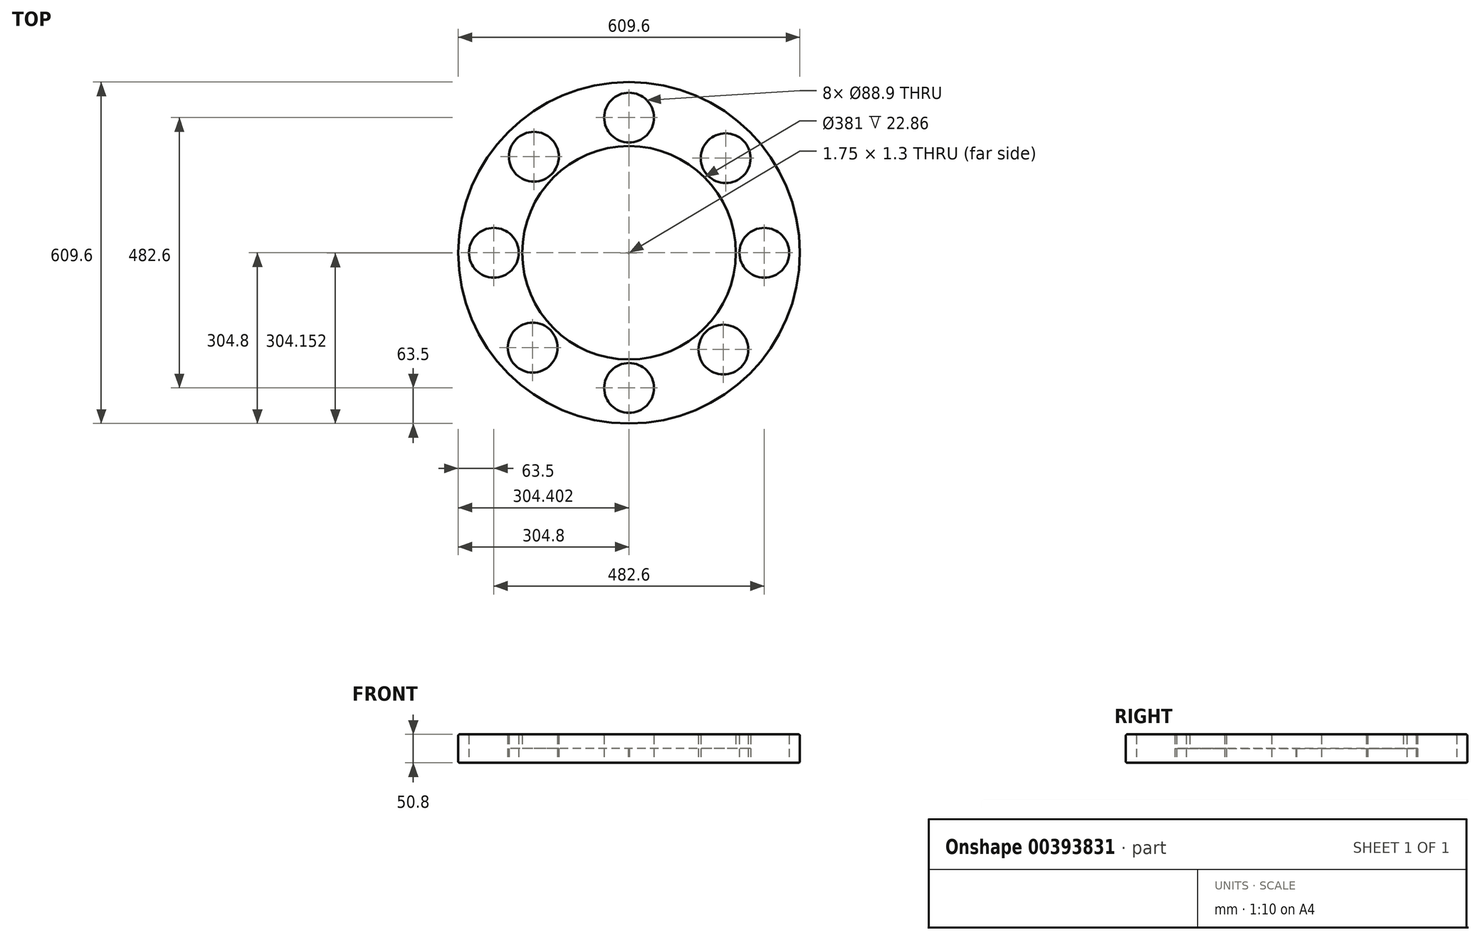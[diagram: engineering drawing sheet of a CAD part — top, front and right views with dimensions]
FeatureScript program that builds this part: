
annotation { "Feature Type Name" : "Feature", "Feature Type Description" : "" }
export const myFeature = defineFeature(function(context is Context, id is Id, definition is map)
    precondition{}
    {
        {
            var Q0;
            Q0=qCreatedBy(makeId("Top.planeOp"),FACE);
            var sketch = newSketch(context, id + "F0", { "sketchPlane" : qUnion([Q0])});
            skCircle(sketch, "E0", {"center": v(0, 0) * mm, "radius": 304.8 * mm});
            skCircle(sketch, "E1", {"center": v(0, 0) * mm, "radius": 190.5 * mm});
            skCircle(sketch, "E2", {"center": v(0, 241.3) * mm, "radius": 44.45 * mm});
            skCircle(sketch, "E3", {"center": v(241.3, 0) * mm, "radius": 44.45 * mm});
            skCircle(sketch, "E4", {"center": v(0, -241.3) * mm, "radius": 44.45 * mm});
            skCircle(sketch, "E5", {"center": v(-241.3, 0) * mm, "radius": 44.45 * mm});
            skCircle(sketch, "E6", {"center": v(-169.71, 171.53) * mm, "radius": 44.45 * mm});
            skCircle(sketch, "E7", {"center": v(172.4, 168.83) * mm, "radius": 44.45 * mm});
            skCircle(sketch, "E8", {"center": v(168.42, -172.8) * mm, "radius": 44.45 * mm});
            skCircle(sketch, "E9", {"center": v(-171.93, -169.3) * mm, "radius": 44.45 * mm});
            skLineSegment(sketch, "E10", {"start": v(0, 241.3) * mm, "end": v(0, 304.8) * mm});
            skLineSegment(sketch, "E11", {"start": v(241.3, 0) * mm, "end": v(304.8, 0) * mm});
            skLineSegment(sketch, "E12", {"start": v(0, -241.3) * mm, "end": v(0, -304.8) * mm});
            skLineSegment(sketch, "E13", {"start": v(-241.3, 0) * mm, "end": v(-304.8, 0) * mm});
            skLineSegment(sketch, "E14", {"start": v(0, 304.8) * mm, "end": v(0, -304.8) * mm});
            skLineSegment(sketch, "E15", {"start": v(-304.8, 0) * mm, "end": v(304.8, 0) * mm});
            skLineSegment(sketch, "E16", {"start": v(-169.71, 171.53) * mm, "end": v(168.42, -172.8) * mm});
            skLineSegment(sketch, "E17", {"start": v(172.4, 168.83) * mm, "end": v(-171.93, -169.3) * mm});
            skSolve(sketch);
        }
        {
            var Q0;
            Q0 = qSketchRegion(id + "F0", true);
            extrude(context, id + "F1", {"entities" : qUnion([Q0]), "depth" : 50.8 * mm});
        }
        {
            var Q0;
            Q0=makeQuery(id+"F0.imprint","IMPRINT",FACE,{"disambiguationData":[TD([[makeQuery(id+"F0.imprint","IMPRINT",EDGE,{"derivedFrom":sQuery(id+"F0.wireOp",EDGE,"E9")}),1.0]])]});
            var Q1;
            {var subQ0=sQuery(id+"F0.wireOp",EDGE,"E15");var subQ4=makeQuery(id+"F0.imprint","IMPRINT",VERTEX,{"disambiguationData":[OD(0.0)],"derivedFrom":subQ0});Q1=makeQuery(id+"F0.imprint","IMPRINT",FACE,{"disambiguationData":[TD([[makeQuery(id+"F0.imprint","IMPRINT",EDGE,{"disambiguationData":[TD([[subQ4,1.0]])],"derivedFrom":subQ0}),-1.0]])]});}
            var Q2;
            {var subQ0=sQuery(id+"F0.wireOp",EDGE,"E15");var subQ4=makeQuery(id+"F0.imprint","IMPRINT",VERTEX,{"disambiguationData":[OD(0.0)],"derivedFrom":subQ0});Q2=makeQuery(id+"F0.imprint","IMPRINT",FACE,{"disambiguationData":[TD([[makeQuery(id+"F0.imprint","IMPRINT",EDGE,{"disambiguationData":[TD([[subQ4,1.0]])],"derivedFrom":subQ0}),1.0]])]});}
            var Q3;
            Q3=makeQuery(id+"F0.imprint","IMPRINT",FACE,{"disambiguationData":[TD([[makeQuery(id+"F0.imprint","IMPRINT",EDGE,{"derivedFrom":sQuery(id+"F0.wireOp",EDGE,"E6")}),1.0]])]});
            var Q4;
            {var subQ0=sQuery(id+"F0.wireOp",EDGE,"E14");var subQ4=makeQuery(id+"F0.imprint","IMPRINT",VERTEX,{"disambiguationData":[OD(0.0)],"derivedFrom":subQ0});Q4=makeQuery(id+"F0.imprint","IMPRINT",FACE,{"disambiguationData":[TD([[makeQuery(id+"F0.imprint","IMPRINT",EDGE,{"disambiguationData":[TD([[subQ4,1.0]])],"derivedFrom":subQ0}),-1.0]])]});}
            var Q5;
            {var subQ0=sQuery(id+"F0.wireOp",EDGE,"E14");var subQ4=makeQuery(id+"F0.imprint","IMPRINT",VERTEX,{"disambiguationData":[OD(0.0)],"derivedFrom":subQ0});Q5=makeQuery(id+"F0.imprint","IMPRINT",FACE,{"disambiguationData":[TD([[makeQuery(id+"F0.imprint","IMPRINT",EDGE,{"disambiguationData":[TD([[subQ4,1.0]])],"derivedFrom":subQ0}),1.0]])]});}
            var Q6;
            Q6=makeQuery(id+"F0.imprint","IMPRINT",FACE,{"disambiguationData":[TD([[makeQuery(id+"F0.imprint","IMPRINT",EDGE,{"derivedFrom":sQuery(id+"F0.wireOp",EDGE,"E7")}),1.0]])]});
            var Q7;
            {var subQ0=sQuery(id+"F0.wireOp",EDGE,"E15");var subQ4=makeQuery(id+"F0.imprint","IMPRINT",VERTEX,{"disambiguationData":[OD(1.0)],"derivedFrom":subQ0});Q7=makeQuery(id+"F0.imprint","IMPRINT",FACE,{"disambiguationData":[TD([[makeQuery(id+"F0.imprint","IMPRINT",EDGE,{"disambiguationData":[TD([[subQ4,1.0]])],"derivedFrom":subQ0}),1.0]])]});}
            var Q8;
            {var subQ0=sQuery(id+"F0.wireOp",EDGE,"E15");var subQ4=makeQuery(id+"F0.imprint","IMPRINT",VERTEX,{"disambiguationData":[OD(1.0)],"derivedFrom":subQ0});Q8=makeQuery(id+"F0.imprint","IMPRINT",FACE,{"disambiguationData":[TD([[makeQuery(id+"F0.imprint","IMPRINT",EDGE,{"disambiguationData":[TD([[subQ4,1.0]])],"derivedFrom":subQ0}),-1.0]])]});}
            var Q9;
            Q9=makeQuery(id+"F0.imprint","IMPRINT",FACE,{"disambiguationData":[TD([[makeQuery(id+"F0.imprint","IMPRINT",EDGE,{"derivedFrom":sQuery(id+"F0.wireOp",EDGE,"E8")}),1.0]])]});
            var Q10;
            {var subQ0=sQuery(id+"F0.wireOp",EDGE,"E14");var subQ4=makeQuery(id+"F0.imprint","IMPRINT",VERTEX,{"disambiguationData":[OD(1.0)],"derivedFrom":subQ0});Q10=makeQuery(id+"F0.imprint","IMPRINT",FACE,{"disambiguationData":[TD([[makeQuery(id+"F0.imprint","IMPRINT",EDGE,{"disambiguationData":[TD([[subQ4,1.0]])],"derivedFrom":subQ0}),1.0]])]});}
            var Q11;
            {var subQ0=sQuery(id+"F0.wireOp",EDGE,"E14");var subQ4=makeQuery(id+"F0.imprint","IMPRINT",VERTEX,{"disambiguationData":[OD(1.0)],"derivedFrom":subQ0});Q11=makeQuery(id+"F0.imprint","IMPRINT",FACE,{"disambiguationData":[TD([[makeQuery(id+"F0.imprint","IMPRINT",EDGE,{"disambiguationData":[TD([[subQ4,1.0]])],"derivedFrom":subQ0}),-1.0]])]});}
            var Q12;
            Q12=sQuery(id+"F0.wireOp",EDGE,"E5");
            var Q13;
            Q13=sQuery(id+"F0.wireOp",EDGE,"E6");
            var Q14;
            Q14=sQuery(id+"F0.wireOp",EDGE,"E2");
            var Q15;
            Q15=sQuery(id+"F0.wireOp",EDGE,"E7");
            var Q16;
            Q16=sQuery(id+"F0.wireOp",EDGE,"E3");
            var Q17;
            Q17=sQuery(id+"F0.wireOp",EDGE,"E8");
            var Q18;
            Q18=sQuery(id+"F0.wireOp",EDGE,"E4");
            var Q19;
            Q19=sQuery(id+"F0.wireOp",EDGE,"E9");
            extrude(context, id + "F2", {"entities" : qUnion([Q0, Q1, Q2, Q3, Q4, Q5, Q6, Q7, Q8, Q9, Q10, Q11]), "surfaceEntities" : qUnion([Q12, Q13, Q14, Q15, Q16, Q17, Q18, Q19]), "depth" : 25.4 * mm});
        }
        {
            var Q0;
            {var subQ0=sQuery(id+"F0.wireOp",EDGE,"E17");var subQ1=sQuery(id+"F0.wireOp",EDGE,"E1");var subQ2=makeQuery(id+"F0.imprint","INTERSECT",VERTEX,{"disambiguationData":[OD(1.0)],"derivedFrom":[subQ1,subQ0]});Q0=makeQuery(id+"F0.imprint","IMPRINT",FACE,{"disambiguationData":[TD([[makeQuery(id+"F0.imprint","IMPRINT",EDGE,{"disambiguationData":[TD([[subQ2,1.0]])],"derivedFrom":subQ1}),1.0]])]});}
            var Q1;
            {var subQ0=sQuery(id+"F0.wireOp",EDGE,"E17");var subQ1=sQuery(id+"F0.wireOp",EDGE,"E1");var subQ2=makeQuery(id+"F0.imprint","INTERSECT",VERTEX,{"disambiguationData":[OD(1.0)],"derivedFrom":[subQ1,subQ0]});Q1=makeQuery(id+"F0.imprint","IMPRINT",FACE,{"disambiguationData":[TD([[makeQuery(id+"F0.imprint","IMPRINT",EDGE,{"disambiguationData":[TD([[subQ2,-1.0]])],"derivedFrom":subQ1}),1.0]])]});}
            var Q2;
            {var subQ0=sQuery(id+"F0.wireOp",EDGE,"E16");var subQ1=sQuery(id+"F0.wireOp",EDGE,"E1");var subQ2=makeQuery(id+"F0.imprint","INTERSECT",VERTEX,{"disambiguationData":[OD(1.0)],"derivedFrom":[subQ1,subQ0]});Q2=makeQuery(id+"F0.imprint","IMPRINT",FACE,{"disambiguationData":[TD([[makeQuery(id+"F0.imprint","IMPRINT",EDGE,{"disambiguationData":[TD([[subQ2,1.0]])],"derivedFrom":subQ1}),1.0]])]});}
            var Q3;
            {var subQ1=sQuery(id+"F0.wireOp",EDGE,"E1");var subQ7=sQuery(id+"F0.wireOp",EDGE,"E16");var subQ9=makeQuery(id+"F0.imprint","INTERSECT",VERTEX,{"disambiguationData":[OD(1.0)],"derivedFrom":[subQ1,subQ7]});Q3=makeQuery(id+"F0.imprint","IMPRINT",FACE,{"disambiguationData":[TD([[makeQuery(id+"F0.imprint","IMPRINT",EDGE,{"disambiguationData":[TD([[subQ9,-1.0]])],"derivedFrom":subQ1}),1.0]])]});}
            var Q4;
            {var subQ0=sQuery(id+"F0.wireOp",EDGE,"E17");var subQ1=sQuery(id+"F0.wireOp",EDGE,"E1");var subQ2=makeQuery(id+"F0.imprint","INTERSECT",VERTEX,{"disambiguationData":[OD(0.0)],"derivedFrom":[subQ1,subQ0]});Q4=makeQuery(id+"F0.imprint","IMPRINT",FACE,{"disambiguationData":[TD([[makeQuery(id+"F0.imprint","IMPRINT",EDGE,{"disambiguationData":[TD([[subQ2,1.0]])],"derivedFrom":subQ1}),1.0]])]});}
            var Q5;
            {var subQ0=sQuery(id+"F0.wireOp",EDGE,"E17");var subQ1=sQuery(id+"F0.wireOp",EDGE,"E1");var subQ2=makeQuery(id+"F0.imprint","INTERSECT",VERTEX,{"disambiguationData":[OD(0.0)],"derivedFrom":[subQ1,subQ0]});Q5=makeQuery(id+"F0.imprint","IMPRINT",FACE,{"disambiguationData":[TD([[makeQuery(id+"F0.imprint","IMPRINT",EDGE,{"disambiguationData":[TD([[subQ2,-1.0]])],"derivedFrom":subQ1}),1.0]])]});}
            var Q6;
            {var subQ0=sQuery(id+"F0.wireOp",EDGE,"E16");var subQ1=sQuery(id+"F0.wireOp",EDGE,"E1");var subQ2=makeQuery(id+"F0.imprint","INTERSECT",VERTEX,{"disambiguationData":[OD(0.0)],"derivedFrom":[subQ1,subQ0]});Q6=makeQuery(id+"F0.imprint","IMPRINT",FACE,{"disambiguationData":[TD([[makeQuery(id+"F0.imprint","IMPRINT",EDGE,{"disambiguationData":[TD([[subQ2,1.0]])],"derivedFrom":subQ1}),1.0]])]});}
            var Q7;
            {var subQ0=sQuery(id+"F0.wireOp",EDGE,"E16");var subQ1=sQuery(id+"F0.wireOp",EDGE,"E1");var subQ2=makeQuery(id+"F0.imprint","INTERSECT",VERTEX,{"disambiguationData":[OD(0.0)],"derivedFrom":[subQ1,subQ0]});Q7=makeQuery(id+"F0.imprint","IMPRINT",FACE,{"disambiguationData":[TD([[makeQuery(id+"F0.imprint","IMPRINT",EDGE,{"disambiguationData":[TD([[subQ2,-1.0]])],"derivedFrom":subQ1}),1.0]])]});}
            extrude(context, id + "F3", {"entities" : qUnion([Q0, Q1, Q2, Q3, Q4, Q5, Q6, Q7]), "operationType" : NewBodyOperationType.ADD, "depth" : 25.4 * mm});
        }
        {
            var Q0;
            Q0=makeQuery(id+"F1.opExtrude","CAP_FACE",FACE,{"disambiguationData":[OSD([sQuery(id+"F0.wireOp",EDGE,"E0"),sQuery(id+"F0.wireOp",EDGE,"E1"),sQuery(id+"F0.wireOp",EDGE,"E2"),sQuery(id+"F0.wireOp",EDGE,"E3"),sQuery(id+"F0.wireOp",EDGE,"E4"),sQuery(id+"F0.wireOp",EDGE,"E5"),sQuery(id+"F0.wireOp",EDGE,"E6"),sQuery(id+"F0.wireOp",EDGE,"E7"),sQuery(id+"F0.wireOp",EDGE,"E8"),sQuery(id+"F0.wireOp",EDGE,"E9")])],"isStart":false});
            var Q1;
            Q1=makeQuery(id+"F1.opExtrude","CAP_EDGE",EDGE,{"disambiguationData":[OSD([sQuery(id+"F0.wireOp",EDGE,"E0")])],"isStart":true});
            fillet(context, id + "F4", {"entities" : qUnion([Q0, Q1]), "radius" : 2.54 * mm, "tangentPropagation" : true, "allowEdgeOverflow" : false});
        }
    });
